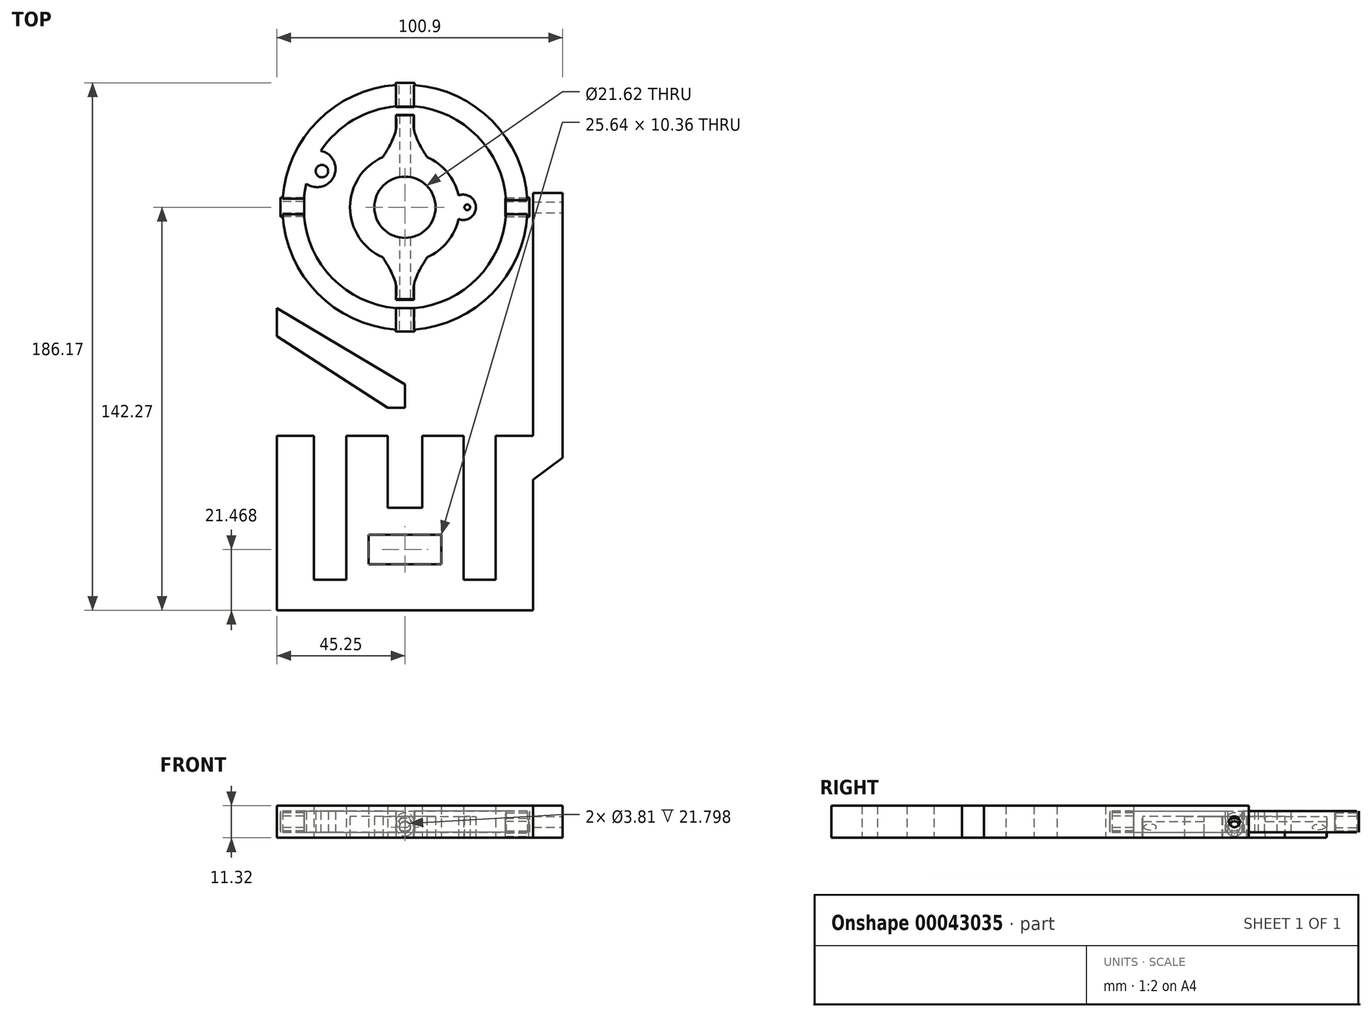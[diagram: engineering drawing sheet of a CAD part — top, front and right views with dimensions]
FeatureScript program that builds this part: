
annotation { "Feature Type Name" : "Feature", "Feature Type Description" : "" }
export const myFeature = defineFeature(function(context is Context, id is Id, definition is map)
    precondition{}
    {
        {
            var Q0;
            Q0=qCreatedBy(makeId("Top.planeOp"),FACE);
            var sketch = newSketch(context, id + "F0", { "sketchPlane" : qUnion([Q0])});
            skCircle(sketch, "E0", {"center": v(0, 0) * mm, "radius": 43.3 * mm});
            skCircle(sketch, "E1", {"center": v(0, 0) * mm, "radius": 35.8 * mm});
            skCircle(sketch, "E2", {"center": v(0, 0) * mm, "radius": 19.37 * mm});
            skCircle(sketch, "E3", {"center": v(0, 0) * mm, "radius": 10.81 * mm});
            skFitSpline(sketch, "E4", {"points": [v(-7.8, 17.73) * mm, v(-3.24, 27.17) * mm, v(-3.2, 32.44) * mm], "startDerivative": vector(10.8, 16.69) * mm, "endDerivative": vector(-0.96, 12.23) * mm});
            skFitSpline(sketch, "E5.MirrorCS", {"points": [v(7.8, 17.73) * mm, v(3.24, 27.17) * mm, v(3.2, 32.44) * mm], "startDerivative": vector(-10.8, 16.69) * mm, "endDerivative": vector(0.96, 12.23) * mm});
            skFitSpline(sketch, "E6.MirrorCS", {"points": [v(7.8, -17.73) * mm, v(3.24, -27.17) * mm, v(3.2, -32.44) * mm], "startDerivative": vector(-10.8, -16.69) * mm, "endDerivative": vector(0.96, -12.23) * mm});
            skFitSpline(sketch, "E7.MirrorCS", {"points": [v(-7.8, -17.73) * mm, v(-3.24, -27.17) * mm, v(-3.2, -32.44) * mm], "startDerivative": vector(10.8, -16.69) * mm, "endDerivative": vector(-0.96, -12.23) * mm});
            skLineSegment(sketch, "E8", {"start": v(-3.2, 32.44) * mm, "end": v(3.2, 32.44) * mm});
            skLineSegment(sketch, "E9", {"start": v(-3.2, -32.44) * mm, "end": v(3.2, -32.44) * mm});
            skArc(sketch, "E10", {"start": v(-34.8, 8.37) * mm, "mid": v(-25.03, 10.98) * mm, "end": v(-29.73, 19.93) * mm});
            skCircle(sketch, "E11", {"center": v(-29.31, 12.76) * mm, "radius": 2.2 * mm});
            skArc(sketch, "E12", {"start": v(18.92, -4.16) * mm, "mid": v(25.04, 0) * mm, "end": v(18.92, 4.16) * mm});
            skCircle(sketch, "E13", {"center": v(22, 0) * mm, "radius": 1 * mm});
            skLineSegment(sketch, "E14", {"start": v(3.2, 43.18) * mm, "end": v(3.2, 35.65) * mm});
            skLineSegment(sketch, "E15", {"start": v(-3.2, 43.18) * mm, "end": v(-3.2, 35.65) * mm});
            skLineSegment(sketch, "E16", {"start": v(-3.2, -35.65) * mm, "end": v(-3.2, -43.18) * mm});
            skLineSegment(sketch, "E17", {"start": v(3.2, -35.65) * mm, "end": v(3.2, -43.18) * mm});
            skLineSegment(sketch, "E18", {"start": v(35.7, 2.55) * mm, "end": v(43.22, 2.55) * mm});
            skLineSegment(sketch, "E19", {"start": v(-35.66, 3.06) * mm, "end": v(-43.18, 3.06) * mm});
            skLineSegment(sketch, "E20", {"start": v(-43.23, -2.4) * mm, "end": v(-35.71, -2.4) * mm});
            skLineSegment(sketch, "E21", {"start": v(35.71, -2.4) * mm, "end": v(43.23, -2.4) * mm});
            skSolve(sketch);
        }
        {
            var Q0;
            Q0=qCreatedBy(makeId("Front.planeOp"),FACE);
            var sketch = newSketch(context, id + "F1", { "sketchPlane" : qUnion([Q0])});
            skCircle(sketch, "E22", {"center": v(0, 0) * mm, "radius": 3.18 * mm});
            skCircle(sketch, "E23", {"center": v(0, 0) * mm, "radius": 2.03 * mm});
            skSolve(sketch);
        }
        {
            var Q0;
            Q0=makeQuery(id+"F1.imprint","IMPRINT",FACE,{"disambiguationData":[TD([[makeQuery(id+"F1.imprint","IMPRINT",EDGE,{"derivedFrom":sQuery(id+"F1.wireOp",EDGE,"E22")}),1.0]])]});
            extrude(context, id + "F2", {"entities" : qUnion([Q0]), "depth" : 19.43 * mm});
        }
        {
            var Q0;
            Q0=makeQuery(id+"F2.opExtrude","SWEPT_BODY",BODY,{"disambiguationData":[OSD([sQuery(id+"F1.wireOp",EDGE,"E22"),sQuery(id+"F1.wireOp",EDGE,"E23")])]});
            transform(context, id + "F3", {"entities" : qUnion([Q0]), "transformType" : TransformType.TRANSLATION_3D, "dx" : 0 * mm, "dy" : -11.62 * mm, "dz" : 0 * mm, "makeCopy" : false});
        }
        {
            var Q0;
            Q0=makeQuery(id+"F2.opExtrude","SWEPT_BODY",BODY,{"disambiguationData":[OSD([sQuery(id+"F1.wireOp",EDGE,"E22"),sQuery(id+"F1.wireOp",EDGE,"E23")])]});
            var Q1;
            Q1=sQuery(id+"F0.wireOp",EDGE,"E3");
            transform(context, id + "F4", {"entities" : qUnion([Q0]), "transformType" : TransformType.ROTATION, "transformAxis" : qUnion([Q1]), "angle" : 90 * degree, "makeCopy" : true});
        }
        {
            var Q0;
            Q0=makeQuery(id+"F4.opPattern","COPY",FACE,{"derivedFrom":makeQuery(id+"F2.opExtrude","CAP_FACE",FACE,{"disambiguationData":[OSD([sQuery(id+"F1.wireOp",EDGE,"E22"),sQuery(id+"F1.wireOp",EDGE,"E23")])],"isStart":false}),"instanceName":"1"});
            var sketch = newSketch(context, id + "F5", { "sketchPlane" : qUnion([Q0])});
            skCircle(sketch, "E24", {"center": v(0, 0) * mm, "radius": 2.04 * mm});
            skCircle(sketch, "E25", {"center": v(0, 0) * mm, "radius": 3.19 * mm});
            skSolve(sketch);
        }
        {
            var Q0;
            Q0=makeQuery(id+"F5.imprint","IMPRINT",FACE,{"disambiguationData":[TD([[makeQuery(id+"F5.imprint","IMPRINT",EDGE,{"derivedFrom":sQuery(id+"F5.wireOp",EDGE,"E24")}),-1.0]])]});
            extrude(context, id + "F6", {"entities" : qUnion([Q0]), "oppositeDirection" : true, "depth" : 8.32 * mm});
        }
        {
            var Q0;
            Q0=makeQuery(id+"F4.opPattern","COPY",BODY,{"derivedFrom":makeQuery(id+"F2.opExtrude","SWEPT_BODY",BODY,{"disambiguationData":[OSD([sQuery(id+"F1.wireOp",EDGE,"E22"),sQuery(id+"F1.wireOp",EDGE,"E23")])]}),"instanceName":"1"});
            deleteBodies(context, id + "F7", {"entities" : qUnion([Q0])});
        }
        {
            var Q0;
            Q0=makeQuery(id+"F6.opExtrude","SWEPT_BODY",BODY,{"disambiguationData":[OSD([sQuery(id+"F1.wireOp",EDGE,"E22"),sQuery(id+"F5.wireOp",EDGE,"E24")])]});
            var Q1;
            Q1=qCreatedBy(makeId("Right.planeOp"),FACE);
            mirror(context, id + "F8", {"entities" : qUnion([Q0]), "mirrorPlane" : qUnion([Q1])});
        }
        {
            var Q0;
            Q0=makeQuery(id+"F2.opExtrude","SWEPT_BODY",BODY,{"disambiguationData":[OSD([sQuery(id+"F1.wireOp",EDGE,"E22"),sQuery(id+"F1.wireOp",EDGE,"E23")])]});
            var Q1;
            Q1=qCreatedBy(makeId("Front.planeOp"),FACE);
            mirror(context, id + "F9", {"entities" : qUnion([Q0]), "mirrorPlane" : qUnion([Q1])});
        }
        {
            var Q0;
            Q0=makeQuery(id+"F8.opPattern","COPY",BODY,{"derivedFrom":makeQuery(id+"F6.opExtrude","SWEPT_BODY",BODY,{"disambiguationData":[OSD([sQuery(id+"F1.wireOp",EDGE,"E22"),sQuery(id+"F5.wireOp",EDGE,"E24")])]}),"instanceName":"1"});
            transform(context, id + "F10", {"entities" : qUnion([Q0]), "transformType" : TransformType.TRANSLATION_3D, "dx" : -12.85 * mm, "dy" : 0 * mm, "dz" : 0 * mm, "makeCopy" : false});
        }
        {
            var Q0;
            Q0=makeQuery(id+"F6.opExtrude","SWEPT_BODY",BODY,{"disambiguationData":[OSD([sQuery(id+"F1.wireOp",EDGE,"E22"),sQuery(id+"F5.wireOp",EDGE,"E24")])]});
            transform(context, id + "F11", {"entities" : qUnion([Q0]), "transformType" : TransformType.TRANSLATION_3D, "dx" : 12.67 * mm, "dy" : 0 * mm, "dz" : 0 * mm, "makeCopy" : false});
        }
        {
            var Q0;
            Q0=makeQuery(id+"F9.opPattern","COPY",BODY,{"derivedFrom":makeQuery(id+"F2.opExtrude","SWEPT_BODY",BODY,{"disambiguationData":[OSD([sQuery(id+"F1.wireOp",EDGE,"E22"),sQuery(id+"F1.wireOp",EDGE,"E23")])]}),"instanceName":"1"});
            transform(context, id + "F12", {"entities" : qUnion([Q0]), "transformType" : TransformType.TRANSLATION_3D, "dx" : 0 * mm, "dy" : 1.58 * mm, "dz" : 0 * mm, "makeCopy" : false});
        }
        {
            var Q0;
            Q0=makeQuery(id+"F2.opExtrude","SWEPT_BODY",BODY,{"disambiguationData":[OSD([sQuery(id+"F1.wireOp",EDGE,"E22"),sQuery(id+"F1.wireOp",EDGE,"E23")])]});
            transform(context, id + "F13", {"entities" : qUnion([Q0]), "transformType" : TransformType.TRANSLATION_3D, "dx" : 0 * mm, "dy" : -2.1 * mm, "dz" : 0 * mm, "makeCopy" : false});
        }
        {
            var Q0;
            Q0=makeQuery(id+"F8.opPattern","COPY",BODY,{"derivedFrom":makeQuery(id+"F6.opExtrude","SWEPT_BODY",BODY,{"disambiguationData":[OSD([sQuery(id+"F1.wireOp",EDGE,"E22"),sQuery(id+"F5.wireOp",EDGE,"E24")])]}),"instanceName":"1"});
            var Q1;
            Q1=makeQuery(id+"F6.opExtrude","SWEPT_BODY",BODY,{"disambiguationData":[OSD([sQuery(id+"F1.wireOp",EDGE,"E22"),sQuery(id+"F5.wireOp",EDGE,"E24")])]});
            var Q2;
            Q2=sQuery(id+"F0.wireOp",EDGE,"E3");
            transform(context, id + "F14", {"entities" : qUnion([Q0, Q1]), "transformType" : TransformType.ROTATION, "transformAxis" : qUnion([Q2]), "angle" : 90 * degree, "makeCopy" : true});
        }
        {
            var Q0;
            {var subQ2=sQuery(id+"F0.wireOp",EDGE,"E15");Q0=makeQuery(id+"F0.imprint","IMPRINT",FACE,{"disambiguationData":[TD([[makeQuery(id+"F0.imprint","IMPRINT",EDGE,{"derivedFrom":subQ2}),-1.0]])]});}
            var Q1;
            {var subQ2=sQuery(id+"F0.wireOp",EDGE,"E16");Q1=makeQuery(id+"F0.imprint","IMPRINT",FACE,{"disambiguationData":[TD([[makeQuery(id+"F0.imprint","IMPRINT",EDGE,{"derivedFrom":subQ2}),-1.0]])]});}
            var Q2;
            {var subQ1=sQuery(id+"F0.wireOp",EDGE,"E17");Q2=makeQuery(id+"F0.imprint","IMPRINT",FACE,{"disambiguationData":[TD([[makeQuery(id+"F0.imprint","IMPRINT",EDGE,{"derivedFrom":subQ1}),1.0]])]});}
            var Q3;
            {var subQ0=sQuery(id+"F0.wireOp",EDGE,"E14");Q3=makeQuery(id+"F0.imprint","IMPRINT",FACE,{"disambiguationData":[TD([[makeQuery(id+"F0.imprint","IMPRINT",EDGE,{"derivedFrom":subQ0}),1.0]])]});}
            var Q4;
            Q4=makeQuery(id+"F0.imprint","IMPRINT",FACE,{"disambiguationData":[TD([[makeQuery(id+"F0.imprint","IMPRINT",EDGE,{"derivedFrom":sQuery(id+"F0.wireOp",EDGE,"E3")}),-1.0]])]});
            var Q5;
            {var subQ0=sQuery(id+"F0.wireOp",EDGE,"E12");Q5=makeQuery(id+"F0.imprint","IMPRINT",FACE,{"disambiguationData":[TD([[makeQuery(id+"F0.imprint","IMPRINT",EDGE,{"derivedFrom":subQ0}),1.0]])]});}
            var Q6;
            {var subQ0=sQuery(id+"F0.wireOp",EDGE,"E10");Q6=makeQuery(id+"F0.imprint","IMPRINT",FACE,{"disambiguationData":[TD([[makeQuery(id+"F0.imprint","IMPRINT",EDGE,{"derivedFrom":subQ0}),1.0]])]});}
            var Q7;
            {var subQ1=sQuery(id+"F0.wireOp",EDGE,"E4");Q7=makeQuery(id+"F0.imprint","IMPRINT",FACE,{"disambiguationData":[TD([[makeQuery(id+"F0.imprint","IMPRINT",EDGE,{"derivedFrom":subQ1}),-1.0]])]});}
            var Q8;
            {var subQ1=sQuery(id+"F0.wireOp",EDGE,"E6.MirrorCS");Q8=makeQuery(id+"F0.imprint","IMPRINT",FACE,{"disambiguationData":[TD([[makeQuery(id+"F0.imprint","IMPRINT",EDGE,{"derivedFrom":subQ1}),-1.0]])]});}
            extrude(context, id + "F15", {"entities" : qUnion([Q0, Q1, Q2, Q3, Q4, Q5, Q6, Q7, Q8]), "endBound" : BoundingType.SYMMETRIC, "depth" : 7.5 * mm});
        }
        {
            var Q0;
            Q0=makeQuery(id+"F14.opPattern","COPY",FACE,{"derivedFrom":makeQuery(id+"F8.opPattern","COPY",FACE,{"derivedFrom":makeQuery(id+"F6.opExtrude","CAP_FACE",FACE,{"disambiguationData":[OSD([sQuery(id+"F1.wireOp",EDGE,"E22"),sQuery(id+"F5.wireOp",EDGE,"E24")])],"isStart":true}),"instanceName":"1"}),"instanceName":"1"});
            var sketch = newSketch(context, id + "F16", { "sketchPlane" : qUnion([Q0])});
            skLineSegment(sketch, "E26.bottom", {"start": v(-3.34, 3.73) * mm, "end": v(3.4, 3.73) * mm});
            skLineSegment(sketch, "E26.top", {"start": v(-3.34, -3.74) * mm, "end": v(3.4, -3.74) * mm});
            skLineSegment(sketch, "E26.left", {"start": v(-3.34, 3.73) * mm, "end": v(-3.34, -3.74) * mm});
            skLineSegment(sketch, "E26.right", {"start": v(3.4, 3.73) * mm, "end": v(3.4, -3.74) * mm});
            skCircle(sketch, "E27", {"center": v(0, 0) * mm, "radius": 3.14 * mm});
            skSolve(sketch);
        }
        {
            var Q0;
            Q0=makeQuery(id+"F16.imprint","IMPRINT",FACE,{"disambiguationData":[TD([[makeQuery(id+"F16.imprint","IMPRINT",EDGE,{"derivedFrom":sQuery(id+"F16.wireOp",EDGE,"E26.bottom")}),-1.0]])]});
            extrude(context, id + "F17", {"entities" : qUnion([Q0]), "oppositeDirection" : true, "depth" : 8.32 * mm});
        }
        {
            var Q0;
            Q0=makeQuery(id+"F17.opExtrude","SWEPT_BODY",BODY,{"disambiguationData":[OSD([sQuery(id+"F1.wireOp",EDGE,"E22"),sQuery(id+"F16.wireOp",EDGE,"E26.bottom"),sQuery(id+"F16.wireOp",EDGE,"E26.top"),sQuery(id+"F16.wireOp",EDGE,"E26.left"),sQuery(id+"F16.wireOp",EDGE,"E26.right")])]});
            var Q1;
            Q1=qCreatedBy(makeId("Front.planeOp"),FACE);
            mirror(context, id + "F18", {"entities" : qUnion([Q0]), "mirrorPlane" : qUnion([Q1])});
        }
        {
            var Q0;
            Q0=makeQuery(id+"F17.opExtrude","SWEPT_BODY",BODY,{"disambiguationData":[OSD([sQuery(id+"F1.wireOp",EDGE,"E22"),sQuery(id+"F16.wireOp",EDGE,"E26.bottom"),sQuery(id+"F16.wireOp",EDGE,"E26.top"),sQuery(id+"F16.wireOp",EDGE,"E26.left"),sQuery(id+"F16.wireOp",EDGE,"E26.right")])]});
            var Q1;
            Q1=makeQuery(id+"F18.opPattern","COPY",BODY,{"derivedFrom":makeQuery(id+"F17.opExtrude","SWEPT_BODY",BODY,{"disambiguationData":[OSD([sQuery(id+"F1.wireOp",EDGE,"E22"),sQuery(id+"F16.wireOp",EDGE,"E26.bottom"),sQuery(id+"F16.wireOp",EDGE,"E26.top"),sQuery(id+"F16.wireOp",EDGE,"E26.left"),sQuery(id+"F16.wireOp",EDGE,"E26.right")])]}),"instanceName":"1"});
            var Q2;
            Q2=sQuery(id+"F0.wireOp",EDGE,"E3");
            transform(context, id + "F19", {"entities" : qUnion([Q0, Q1]), "transformType" : TransformType.ROTATION, "transformAxis" : qUnion([Q2]), "angle" : 90 * degree, "makeCopy" : true});
        }
        {
            var Q0;
            Q0=makeQuery(id+"F2.opExtrude","SWEPT_BODY",BODY,{"disambiguationData":[OSD([sQuery(id+"F1.wireOp",EDGE,"E22"),sQuery(id+"F1.wireOp",EDGE,"E23")])]});
            transform(context, id + "F20", {"entities" : qUnion([Q0]), "transformType" : TransformType.TRANSLATION_3D, "dx" : 0 * mm, "dy" : 0.53 * mm, "dz" : 0 * mm, "makeCopy" : false});
        }
        {
            var Q0;
            Q0=makeQuery(id+"F2.opExtrude","SWEPT_BODY",BODY,{"disambiguationData":[OSD([sQuery(id+"F1.wireOp",EDGE,"E22"),sQuery(id+"F1.wireOp",EDGE,"E23")])]});
            var Q1;
            Q1=makeQuery(id+"F9.opPattern","COPY",BODY,{"derivedFrom":makeQuery(id+"F2.opExtrude","SWEPT_BODY",BODY,{"disambiguationData":[OSD([sQuery(id+"F1.wireOp",EDGE,"E22"),sQuery(id+"F1.wireOp",EDGE,"E23")])]}),"instanceName":"1"});
            var Q2;
            Q2=makeQuery(id+"F15.opExtrude","SWEPT_BODY",BODY,{"disambiguationData":[OSD([sQuery(id+"F0.wireOp",EDGE,"E2"),sQuery(id+"F0.wireOp",EDGE,"E3"),sQuery(id+"F0.wireOp",EDGE,"E4"),sQuery(id+"F0.wireOp",EDGE,"E5.MirrorCS"),sQuery(id+"F0.wireOp",EDGE,"E6.MirrorCS"),sQuery(id+"F0.wireOp",EDGE,"E7.MirrorCS"),sQuery(id+"F0.wireOp",EDGE,"E8"),sQuery(id+"F0.wireOp",EDGE,"E9"),sQuery(id+"F0.wireOp",EDGE,"E12"),sQuery(id+"F0.wireOp",EDGE,"E13")])]});
            booleanBodies(context, id + "F21", {"operationType" : BooleanOperationType.UNION, "tools" : qUnion([Q0, Q1, Q2])});
        }
        {
            var Q0;
            Q0=sQuery(id+"F1.wireOp",VERTEX,"E23.center");
            var Q1;
            Q1=makeQuery(id+"F2.opExtrude","SWEPT_BODY",BODY,{"disambiguationData":[OSD([sQuery(id+"F1.wireOp",EDGE,"E22"),sQuery(id+"F1.wireOp",EDGE,"E23")])]});
            hole(context, id + "F22", {"style" : HoleStyle.SIMPLE, "holeDiameter" : 3.8 * mm, "endStyle" : HoleEndStyle.THROUGH, "locations" : qUnion([Q0]), "scope" : qUnion([Q1])});
        }
        {
            var Q0;
            Q0=makeQuery(id+"F21.opBoolean","SPLIT",FACE,{"disambiguationData":[TD([makeQuery(id+"F2.opExtrude","SWEPT_FACE",FACE,{"disambiguationData":[OSD([sQuery(id+"F1.wireOp",EDGE,"E23")])]})])],"derivedFrom":makeQuery(id+"F15.opExtrude","SWEPT_FACE",FACE,{"disambiguationData":[OSD([sQuery(id+"F0.wireOp",EDGE,"E9")])]})});
            var sketch = newSketch(context, id + "F23", { "sketchPlane" : qUnion([Q0])});
            skCircle(sketch, "E28", {"center": v(0, 0) * mm, "radius": 1.92 * mm});
            skSolve(sketch);
        }
        {
            var Q0;
            Q0=sQuery(id+"F23.wireOp",VERTEX,"E28.center");
            var Q1;
            Q1=makeQuery(id+"F2.opExtrude","SWEPT_BODY",BODY,{"disambiguationData":[OSD([sQuery(id+"F1.wireOp",EDGE,"E22"),sQuery(id+"F1.wireOp",EDGE,"E23")])]});
            hole(context, id + "F24", {"style" : HoleStyle.SIMPLE, "holeDiameter" : 3.8 * mm, "endStyle" : HoleEndStyle.THROUGH, "locations" : qUnion([Q0]), "scope" : qUnion([Q1])});
        }
        {
            var Q0;
            Q0=qCreatedBy(makeId("Top.planeOp"),FACE);
            var sketch = newSketch(context, id + "F25", { "sketchPlane" : qUnion([Q0])});
            skLineSegment(sketch, "E29.bottom", {"start": v(-64.32, 5) * mm, "end": v(0, 5) * mm});
            skLineSegment(sketch, "E29.top", {"start": v(-64.32, -131.44) * mm, "end": v(0, -131.44) * mm});
            skLineSegment(sketch, "E29.left", {"start": v(-64.32, 5) * mm, "end": v(-64.32, -131.44) * mm});
            skLineSegment(sketch, "E29.right", {"start": v(0, 5) * mm, "end": v(0, -131.44) * mm});
            skLineSegment(sketch, "E30", {"start": v(-45.25, 5) * mm, "end": v(-45.25, -131.44) * mm});
            skLineSegment(sketch, "E31", {"start": v(-45.25, -35.63) * mm, "end": v(0, -62.57) * mm});
            skLineSegment(sketch, "E32", {"start": v(0, -62.57) * mm, "end": v(0, -69.89) * mm});
            skLineSegment(sketch, "E33.bottom", {"start": v(-45.25, -70.79) * mm, "end": v(0, -70.79) * mm});
            skLineSegment(sketch, "E33.top", {"start": v(-45.25, -80.7) * mm, "end": v(0, -80.7) * mm});
            skLineSegment(sketch, "E33.left", {"start": v(-45.25, -70.79) * mm, "end": v(-45.25, -80.7) * mm});
            skLineSegment(sketch, "E33.right", {"start": v(0, -70.79) * mm, "end": v(0, -80.7) * mm});
            skLineSegment(sketch, "E34.bottom", {"start": v(0, -80.7) * mm, "end": v(-6.14, -80.7) * mm});
            skLineSegment(sketch, "E34.top", {"start": v(0, -106.1) * mm, "end": v(-6.14, -106.1) * mm});
            skLineSegment(sketch, "E34.left", {"start": v(0, -80.7) * mm, "end": v(0, -106.1) * mm});
            skLineSegment(sketch, "E34.right", {"start": v(-6.14, -80.7) * mm, "end": v(-6.14, -106.1) * mm});
            skLineSegment(sketch, "E35.bottom", {"start": v(0, -115.62) * mm, "end": v(-12.82, -115.62) * mm});
            skLineSegment(sketch, "E35.top", {"start": v(0, -125.98) * mm, "end": v(-12.82, -125.98) * mm});
            skLineSegment(sketch, "E35.left", {"start": v(0, -115.62) * mm, "end": v(0, -125.98) * mm});
            skLineSegment(sketch, "E35.right", {"start": v(-12.82, -115.62) * mm, "end": v(-12.82, -125.98) * mm});
            skLineSegment(sketch, "E36", {"start": v(-20.76, -80.7) * mm, "end": v(-20.76, -131.44) * mm});
            skLineSegment(sketch, "E37", {"start": v(-20.76, -131.44) * mm, "end": v(-32.06, -131.44) * mm});
            skLineSegment(sketch, "E38", {"start": v(-32.06, -131.44) * mm, "end": v(-32.06, -80.7) * mm});
            skLineSegment(sketch, "E39.MirrorCS", {"start": v(64.32, 5) * mm, "end": v(0, 5) * mm});
            skLineSegment(sketch, "E40.MirrorCS", {"start": v(64.32, -131.44) * mm, "end": v(0, -131.44) * mm});
            skLineSegment(sketch, "E41.MirrorCS", {"start": v(0, -125.98) * mm, "end": v(12.82, -125.98) * mm});
            skLineSegment(sketch, "E42.MirrorCS", {"start": v(12.82, -115.62) * mm, "end": v(12.82, -125.98) * mm});
            skLineSegment(sketch, "E43.MirrorCS", {"start": v(0, -115.62) * mm, "end": v(12.82, -115.62) * mm});
            skLineSegment(sketch, "E44.MirrorCS", {"start": v(0, -106.1) * mm, "end": v(6.14, -106.1) * mm});
            skLineSegment(sketch, "E45.MirrorCS", {"start": v(6.14, -80.7) * mm, "end": v(6.14, -106.1) * mm});
            skLineSegment(sketch, "E46.MirrorCS", {"start": v(20.76, -80.7) * mm, "end": v(20.76, -131.44) * mm});
            skLineSegment(sketch, "E47.MirrorCS", {"start": v(32.06, -131.44) * mm, "end": v(32.06, -80.7) * mm});
            skLineSegment(sketch, "E48.MirrorCS", {"start": v(45.25, -80.7) * mm, "end": v(0, -80.7) * mm});
            skLineSegment(sketch, "E49.MirrorCS", {"start": v(45.25, -70.79) * mm, "end": v(0, -70.79) * mm});
            skLineSegment(sketch, "E50.MirrorCS", {"start": v(45.25, -35.63) * mm, "end": v(0, -62.57) * mm});
            skLineSegment(sketch, "E51.MirrorCS", {"start": v(64.32, 5) * mm, "end": v(64.32, -131.44) * mm});
            skLineSegment(sketch, "E52.MirrorCS", {"start": v(45.25, 5) * mm, "end": v(45.25, -131.44) * mm});
            skLineSegment(sketch, "E53", {"start": v(-55.65, 5) * mm, "end": v(-55.65, -131.44) * mm});
            skLineSegment(sketch, "E54.MirrorCS", {"start": v(55.65, 5) * mm, "end": v(55.65, -131.44) * mm});
            skLineSegment(sketch, "E55", {"start": v(-45.25, -45.45) * mm, "end": v(-6.12, -70.79) * mm});
            skLineSegment(sketch, "E56.MirrorCS", {"start": v(45.25, -45.45) * mm, "end": v(6.12, -70.79) * mm});
            skLineSegment(sketch, "E57.bottom", {"start": v(-55.65, -131.44) * mm, "end": v(55.56, -131.44) * mm});
            skLineSegment(sketch, "E57.top", {"start": v(-55.65, -142.27) * mm, "end": v(55.56, -142.27) * mm});
            skLineSegment(sketch, "E57.left", {"start": v(-55.65, -131.44) * mm, "end": v(-55.65, -142.27) * mm});
            skLineSegment(sketch, "E57.right", {"start": v(55.56, -131.44) * mm, "end": v(55.56, -142.27) * mm});
            skLineSegment(sketch, "E58", {"start": v(-32.06, -106.07) * mm, "end": v(-55.65, -88.43) * mm});
            skLineSegment(sketch, "E59.MirrorCS", {"start": v(32.06, -106.07) * mm, "end": v(55.65, -88.43) * mm});
            skLineSegment(sketch, "E60", {"start": v(-45.25, -131.44) * mm, "end": v(-45.25, -142.27) * mm});
            skLineSegment(sketch, "E61", {"start": v(45.25, -131.44) * mm, "end": v(45.25, -142.27) * mm});
            skSolve(sketch);
        }
        {
            var Q0;
            {var subQ5=sQuery(id+"F25.wireOp",EDGE,"E33.left");Q0=makeQuery(id+"F25.imprint","IMPRINT",FACE,{"disambiguationData":[TD([[makeQuery(id+"F25.imprint","IMPRINT",EDGE,{"derivedFrom":subQ5}),-1.0]])]});}
            var Q1;
            {var subQ6=sQuery(id+"F25.wireOp",EDGE,"E31");Q1=makeQuery(id+"F25.imprint","IMPRINT",FACE,{"disambiguationData":[TD([[makeQuery(id+"F25.imprint","IMPRINT",EDGE,{"derivedFrom":subQ6}),-1.0]])]});}
            var Q2;
            {var subQ6=sQuery(id+"F25.wireOp",EDGE,"E32");Q2=makeQuery(id+"F25.imprint","IMPRINT",FACE,{"disambiguationData":[TD([[makeQuery(id+"F25.imprint","IMPRINT",EDGE,{"derivedFrom":subQ6}),1.0]])]});}
            var Q3;
            {var subQ2=sQuery(id+"F25.wireOp",EDGE,"E33.right");Q3=makeQuery(id+"F25.imprint","IMPRINT",FACE,{"disambiguationData":[TD([[makeQuery(id+"F25.imprint","IMPRINT",EDGE,{"derivedFrom":subQ2}),1.0]])]});}
            var Q4;
            {var subQ2=sQuery(id+"F25.wireOp",EDGE,"E33.left");Q4=makeQuery(id+"F25.imprint","IMPRINT",FACE,{"disambiguationData":[TD([[makeQuery(id+"F25.imprint","IMPRINT",EDGE,{"derivedFrom":subQ2}),1.0]])]});}
            var Q5;
            {var subQ3=sQuery(id+"F25.wireOp",EDGE,"E38");var subQ5=sQuery(id+"F25.wireOp",EDGE,"E33.top");var subQ6=makeQuery(id+"F25.imprint","INTERSECT",VERTEX,{"derivedFrom":[subQ5,subQ3]});Q5=makeQuery(id+"F25.imprint","IMPRINT",FACE,{"disambiguationData":[TD([[makeQuery(id+"F25.imprint","IMPRINT",EDGE,{"disambiguationData":[TD([[subQ6,1.0]])],"derivedFrom":subQ3}),1.0]])]});}
            var Q6;
            {var subQ3=sQuery(id+"F25.wireOp",EDGE,"E38");var subQ5=sQuery(id+"F25.wireOp",EDGE,"E57.bottom");var subQ6=makeQuery(id+"F25.imprint","INTERSECT",VERTEX,{"derivedFrom":[subQ3,subQ5]});Q6=makeQuery(id+"F25.imprint","IMPRINT",FACE,{"disambiguationData":[TD([[makeQuery(id+"F25.imprint","IMPRINT",EDGE,{"disambiguationData":[TD([[subQ6,-1.0]])],"derivedFrom":subQ3}),1.0]])]});}
            var Q7;
            {var subQ8=sQuery(id+"F25.wireOp",EDGE,"E34.top");Q7=makeQuery(id+"F25.imprint","IMPRINT",FACE,{"disambiguationData":[TD([[makeQuery(id+"F25.imprint","IMPRINT",EDGE,{"derivedFrom":subQ8}),1.0]])]});}
            var Q8;
            {var subQ9=sQuery(id+"F25.wireOp",EDGE,"E41.MirrorCS");Q8=makeQuery(id+"F25.imprint","IMPRINT",FACE,{"disambiguationData":[TD([[makeQuery(id+"F25.imprint","IMPRINT",EDGE,{"derivedFrom":subQ9}),-1.0]])]});}
            var Q9;
            {var subQ3=sQuery(id+"F25.wireOp",EDGE,"E47.MirrorCS");var subQ5=sQuery(id+"F25.wireOp",EDGE,"E57.bottom");var subQ7=makeQuery(id+"F25.imprint","INTERSECT",VERTEX,{"derivedFrom":[subQ3,subQ5]});Q9=makeQuery(id+"F25.imprint","IMPRINT",FACE,{"disambiguationData":[TD([[makeQuery(id+"F25.imprint","IMPRINT",EDGE,{"disambiguationData":[TD([[subQ7,-1.0]])],"derivedFrom":subQ3}),-1.0]])]});}
            var Q10;
            {var subQ3=sQuery(id+"F25.wireOp",EDGE,"E47.MirrorCS");var subQ5=sQuery(id+"F25.wireOp",EDGE,"E48.MirrorCS");var subQ7=makeQuery(id+"F25.imprint","INTERSECT",VERTEX,{"derivedFrom":[subQ3,subQ5]});Q10=makeQuery(id+"F25.imprint","IMPRINT",FACE,{"disambiguationData":[TD([[makeQuery(id+"F25.imprint","IMPRINT",EDGE,{"disambiguationData":[TD([[subQ7,1.0]])],"derivedFrom":subQ3}),-1.0]])]});}
            var Q11;
            {var subQ1=sQuery(id+"F25.wireOp",EDGE,"E52.MirrorCS");var subQ5=sQuery(id+"F25.wireOp",EDGE,"E39.MirrorCS");var subQ11=makeQuery(id+"F25.imprint","INTERSECT",VERTEX,{"derivedFrom":[subQ5,subQ1]});Q11=makeQuery(id+"F25.imprint","IMPRINT",FACE,{"disambiguationData":[TD([[makeQuery(id+"F25.imprint","IMPRINT",EDGE,{"disambiguationData":[TD([[subQ11,1.0]])],"derivedFrom":subQ5}),1.0]])]});}
            var Q12;
            {var subQ0=sQuery(id+"F25.wireOp",EDGE,"E60");Q12=makeQuery(id+"F25.imprint","IMPRINT",FACE,{"disambiguationData":[TD([[makeQuery(id+"F25.imprint","IMPRINT",EDGE,{"derivedFrom":subQ0}),1.0]])]});}
            extrude(context, id + "F26", {"entities" : qUnion([Q0, Q1, Q2, Q3, Q4, Q5, Q6, Q7, Q8, Q9, Q10, Q11, Q12]), "endBound" : BoundingType.SYMMETRIC, "depth" : 11.32 * mm});
        }
        {
            var Q0;
            Q0=makeQuery(id+"F26.opExtrude","SWEPT_FACE",FACE,{"disambiguationData":[OSD([sQuery(id+"F25.wireOp",EDGE,"E54.MirrorCS")])]});
            var sketch = newSketch(context, id + "F27", { "sketchPlane" : qUnion([Q0])});
            skCircle(sketch, "E62", {"center": v(0, 0) * mm, "radius": 1.88 * mm});
            skSolve(sketch);
        }
        {
            var Q0;
            Q0=sQuery(id+"F27.wireOp",VERTEX,"E62.center");
            var Q1;
            Q1=makeQuery(id+"F26.opExtrude","SWEPT_BODY",BODY,{"disambiguationData":[OSD([sQuery(id+"F25.wireOp",EDGE,"E29.bottom"),sQuery(id+"F25.wireOp",EDGE,"E30"),sQuery(id+"F25.wireOp",EDGE,"E31"),sQuery(id+"F25.wireOp",EDGE,"E33.bottom"),sQuery(id+"F25.wireOp",EDGE,"E33.top"),sQuery(id+"F25.wireOp",EDGE,"E34.bottom"),sQuery(id+"F25.wireOp",EDGE,"E34.top"),sQuery(id+"F25.wireOp",EDGE,"E34.right"),sQuery(id+"F25.wireOp",EDGE,"E35.bottom"),sQuery(id+"F25.wireOp",EDGE,"E35.top"),sQuery(id+"F25.wireOp",EDGE,"E35.right"),sQuery(id+"F25.wireOp",EDGE,"E36"),sQuery(id+"F25.wireOp",EDGE,"E38"),sQuery(id+"F25.wireOp",EDGE,"E39.MirrorCS"),sQuery(id+"F25.wireOp",EDGE,"E40.MirrorCS"),sQuery(id+"F25.wireOp",EDGE,"E41.MirrorCS"),sQuery(id+"F25.wireOp",EDGE,"E42.MirrorCS"),sQuery(id+"F25.wireOp",EDGE,"E43.MirrorCS"),sQuery(id+"F25.wireOp",EDGE,"E44.MirrorCS"),sQuery(id+"F25.wireOp",EDGE,"E45.MirrorCS"),sQuery(id+"F25.wireOp",EDGE,"E46.MirrorCS"),sQuery(id+"F25.wireOp",EDGE,"E47.MirrorCS"),sQuery(id+"F25.wireOp",EDGE,"E48.MirrorCS"),sQuery(id+"F25.wireOp",EDGE,"E49.MirrorCS"),sQuery(id+"F25.wireOp",EDGE,"E50.MirrorCS"),sQuery(id+"F25.wireOp",EDGE,"E52.MirrorCS"),sQuery(id+"F25.wireOp",EDGE,"E53"),sQuery(id+"F25.wireOp",EDGE,"E54.MirrorCS"),sQuery(id+"F25.wireOp",EDGE,"E55"),sQuery(id+"F25.wireOp",EDGE,"E56.MirrorCS"),sQuery(id+"F25.wireOp",EDGE,"E57.bottom"),sQuery(id+"F25.wireOp",EDGE,"E57.top"),sQuery(id+"F25.wireOp",EDGE,"E57.left"),sQuery(id+"F25.wireOp",EDGE,"E57.right")])]});
            hole(context, id + "F28", {"style" : HoleStyle.SIMPLE, "holeDiameter" : 3.8 * mm, "endStyle" : HoleEndStyle.THROUGH, "locations" : qUnion([Q0]), "scope" : qUnion([Q1])});
        }
        {
            var Q0;
            Q0=makeQuery(id+"F6.opExtrude","SWEPT_BODY",BODY,{"disambiguationData":[OSD([sQuery(id+"F1.wireOp",EDGE,"E22"),sQuery(id+"F5.wireOp",EDGE,"E24")])]});
            transform(context, id + "F29", {"entities" : qUnion([Q0]), "transformType" : TransformType.TRANSLATION_3D, "dx" : 0 * mm, "dy" : 0 * mm, "dz" : -1.87 * mm, "makeCopy" : false});
        }
        {
            var Q0;
            Q0=makeQuery(id+"F2.opExtrude","SWEPT_BODY",BODY,{"disambiguationData":[OSD([sQuery(id+"F1.wireOp",EDGE,"E22"),sQuery(id+"F1.wireOp",EDGE,"E23")])]});
            transform(context, id + "F30", {"entities" : qUnion([Q0]), "transformType" : TransformType.TRANSLATION_3D, "dx" : 0 * mm, "dy" : 0 * mm, "dz" : -1.87 * mm, "makeCopy" : false});
        }
    });
